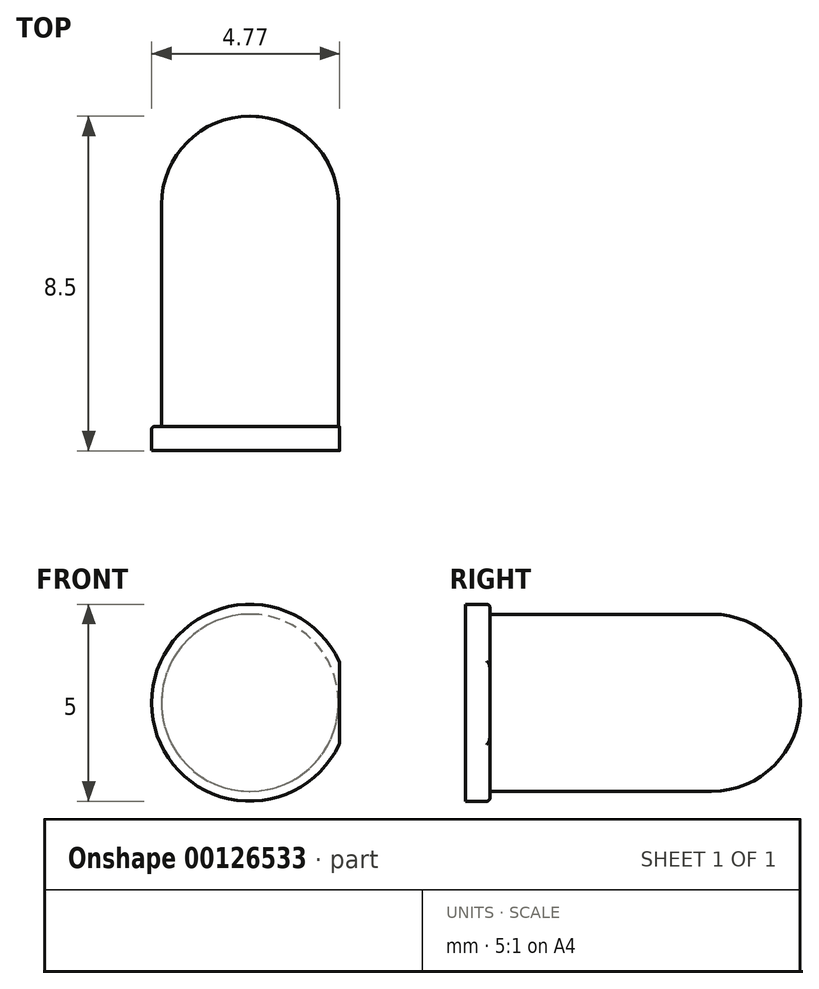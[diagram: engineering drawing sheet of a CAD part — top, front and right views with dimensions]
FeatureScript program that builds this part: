
annotation { "Feature Type Name" : "Feature", "Feature Type Description" : "" }
export const myFeature = defineFeature(function(context is Context, id is Id, definition is map)
    precondition{}
    {
        {
            var Q0;
            Q0=qCreatedBy(makeId("Top.planeOp"),FACE);
            var sketch = newSketch(context, id + "F0", { "sketchPlane" : qUnion([Q0])});
            skLineSegment(sketch, "E0", {"start": v(-101.5, -9.97) * mm, "end": v(-101.5, -18.47) * mm});
            skArc(sketch, "E1", {"start": v(-101.5, -9.97) * mm, "mid": v(-103.75, -12.22) * mm, "end": v(-101.5, -14.47) * mm});
            skLineSegment(sketch, "E2.bottom", {"start": v(-101.5, -18.47) * mm, "end": v(-104, -18.47) * mm});
            skLineSegment(sketch, "E2.top", {"start": v(-101.5, -17.85) * mm, "end": v(-104, -17.85) * mm});
            skLineSegment(sketch, "E2.left", {"start": v(-101.5, -18.47) * mm, "end": v(-101.5, -17.85) * mm});
            skLineSegment(sketch, "E2.right", {"start": v(-104, -18.47) * mm, "end": v(-104, -17.85) * mm});
            skLineSegment(sketch, "E3", {"start": v(-103.75, -12.22) * mm, "end": v(-103.75, -17.85) * mm});
            skSolve(sketch);
        }
        {
            var Q0;
            Q0=qSketchRegion(id+"F0",true);
            var Q1;
            Q1=sQuery(id+"F0.wireOp",EDGE,"E0");
            revolve(context, id + "F1", {"entities" : qUnion([Q0]), "axis" : qUnion([Q1]), "revolveType" : RevolveType.FULL});
        }
        {
            var Q0;
            Q0=qCreatedBy(makeId("Top.planeOp"),FACE);
            var sketch = newSketch(context, id + "F2", { "sketchPlane" : qUnion([Q0])});
            skLineSegment(sketch, "E4.0", {"start": v(-104, -17.85) * mm, "end": v(-99, -17.85) * mm});
            skLineSegment(sketch, "E4.1", {"start": v(-104, -18.47) * mm, "end": v(-99, -18.47) * mm});
            skLineSegment(sketch, "E5", {"start": v(-99, -17.85) * mm, "end": v(-99, -18.47) * mm});
            skLineSegment(sketch, "E6", {"start": v(-99.23, -17.85) * mm, "end": v(-99.23, -18.47) * mm});
            skSolve(sketch);
        }
        {
            var Q0;
            Q0=qSketchRegion(id+"F2",true);
            extrude(context, id + "F3", {"entities" : qUnion([Q0]), "operationType" : NewBodyOperationType.REMOVE, "oppositeDirection" : true, "depth" : 25 * mm, "symmetric" : true});
        }
        {
            var Q0;
            Q0=makeQuery(id+"F1.opRevolve","SWEPT_EDGE",EDGE,{"disambiguationData":[OSD([sQuery(id+"F0.wireOp",EDGE,"E2.top"),sQuery(id+"F0.wireOp",EDGE,"E2.right")])]});
            var Q1;
            Q1=makeQuery(id+"F3.boolean.opBoolean","COPY",EDGE,{"derivedFrom":makeQuery(id+"F3.opExtrude","SWEPT_EDGE",EDGE,{"disambiguationData":[OSD([sQuery(id+"F2.wireOp",EDGE,"E4.0"),sQuery(id+"F2.wireOp",EDGE,"E6")])]})});
            var Q2;
            Q2=makeQuery(id+"F3.boolean.opBoolean","INTERSECT",EDGE,{"disambiguationData":[OD(1.0)],"derivedFrom":[makeQuery(id+"F1.opRevolve","SWEPT_FACE",FACE,{"disambiguationData":[OSD([sQuery(id+"F0.wireOp",EDGE,"E2.right")])]}),makeQuery(id+"F3.opExtrude","SWEPT_FACE",FACE,{"disambiguationData":[OSD([sQuery(id+"F2.wireOp",EDGE,"E6")])]})]});
            var Q3;
            Q3=makeQuery(id+"F3.boolean.opBoolean","INTERSECT",EDGE,{"disambiguationData":[OD(0.0)],"derivedFrom":[makeQuery(id+"F1.opRevolve","SWEPT_FACE",FACE,{"disambiguationData":[OSD([sQuery(id+"F0.wireOp",EDGE,"E2.right")])]}),makeQuery(id+"F3.opExtrude","SWEPT_FACE",FACE,{"disambiguationData":[OSD([sQuery(id+"F2.wireOp",EDGE,"E6")])]})]});
            fillet(context, id + "F4", {"entities" : qUnion([Q0, Q1, Q2, Q3]), "radius" : 0.07 * mm, "tangentPropagation" : true, "allowEdgeOverflow" : false});
        }
    });
